# Revit family: 02-60-0035 DN350 Increased Bore
name_source: partatom
category: Pipe Accessories
units: mm (PartAtom-declared; Revit-internal decimal feet)

## family parameters
Always vertical = Yes
Cut with Voids When Loaded = No
Part Type = Valve - Breaks Into
Round Connector Dimension = Use Diameter
Shared = No
Work Plane-Based = No

## types (2) — shared parameters
1 = 1 mm  [stored 0.00328084 ft]
10 = 10 mm  [stored 0.0328084 ft]
20 = 20 mm  [stored 0.0656168 ft]
5 = 5 mm  [stored 0.0164042 ft]
Body_Arc = 1120 mm
Body_FL_L = 282 mm  [stored 0.925197 ft]
Body_FL_R = 40 mm  [stored 0.131234 ft]
Body_FL_T = 28 mm  [stored 0.0918635 ft]
Body_FL_W = 114 mm  [stored 0.374016 ft]
Body_FL_arc = 1550 mm
Body_FL_rib_dim = 917 mm
Body_FL_rib_dim1 = 251 mm
Body_H = 485 mm
Body_L = 238 mm  [stored 0.78084 ft]
Body_R = 30 mm  [stored 0.0984252 ft]
Body_T = 13 mm
Body_W = 99 mm  [stored 0.324803 ft]
Body_bottom = 208 mm
Bonnet_L = 214 mm  [stored 0.7021 ft]
Bonnet_d1 = 79 mm
Bonnet_d2 = 50 mm  [stored 0.164042 ft]
Bonnet_dim1 = 84 mm  [stored 0.275591 ft]
Bonnet_dim2 = 80 mm  [stored 0.262467 ft]
Bonnet_dim3 = 50 mm  [stored 0.164042 ft]
Bore_R = 175 mm  [stored 0.574147 ft]
DN = 350 mm  [stored 1.14829 ft]
DN350_PN10 = 02-350-60-006
DN350_PN16 = 02-350-60-016
Description_ = AVK GATE VALVE, FLANGED, PN10-16
F = 16 mm  [stored 0.0524934 ft]
F1 = 20 mm  [stored 0.0656168 ft]
F2 = 55 mm  [stored 0.180446 ft]
FL_R = 520 mm
FL_T = 25 mm  [stored 0.082021 ft]
H = 947 mm
H3 = 1207 mm
H3-H = 260 mm  [stored 0.853018 ft]
L = 550 mm
RIB_L = 281 mm  [stored 0.921916 ft]
RIB_L1 = 183 mm
RIB_T = 8 mm  [stored 0.0262467 ft]
Raised_R = 215 mm
Raised_dis = 4 mm  [stored 0.0131234 ft]
Rib1_H = 146 mm
Rib1_L = 282 mm  [stored 0.925197 ft]
Rib1_R = 25 mm  [stored 0.082021 ft]
Rib1_T = 9 mm  [stored 0.0295276 ft]
Rib1_W = 119 mm
Rib2_L = 282 mm  [stored 0.925197 ft]
Rib2_W = 119 mm
Rib3_L = 282 mm  [stored 0.925197 ft]
Rib3_W = 119 mm
Rib_T = 21 mm
Search_table = 02-60-0035 DN350 Increased Bore
Stem = 22 mm  [stored 0.0721785 ft]
Sweep _cut = 5 mm  [stored 0.0164042 ft]
URL_product_pages = https://www.avkvalves.com
W = 282 mm  [stored 0.925197 ft]
Wedge_L = 84 mm  [stored 0.275591 ft]
disk_T = 178 mm
logo_H = 243 mm  [stored 0.797244 ft]
stem1 = 27 mm  [stored 0.0885827 ft]
zero-valued in all types: Default Elevation

## per-type parameters (varying)
| type | Dh | Ds |
| DN350_PN10 | 460 mm | 23 mm  [stored 0.0754593 ft] |
| DN350_PN16 | 470 mm | 28 mm  [stored 0.0918635 ft] |

note: [stored X ft] marks values corroborated as IEEE doubles in the binary element streams (Revit-internal decimal feet)

## geometry (parser evidence)
native form markers: Sweep x5
no freeform markers — native parametric forms only
